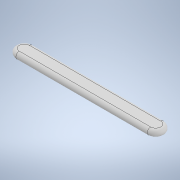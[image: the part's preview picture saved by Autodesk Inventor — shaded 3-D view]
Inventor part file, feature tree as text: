
AUTODESK INVENTOR PART (.ipt)
format: ipt  version: 2020 (Build 240168000, 168)  size: 114,688 bytes
history: native  units: in
note: dims shown in document units (in); Inventor stores cm internally (conversion verified against a paired STEP export)
features: fillet x2, extrude x1, sketch x1
ambient origin geometry x8: Origin, YZ Plane, XZ Plane, XY Plane, X Axis, Y Axis, Z Axis, Center Point
bodies: Solid1 (feature_tree)
feature tree (4):
  extrude  "Extrusion1"  Depth=0.0394in
  fillet  "Fillet1"  Radius=0.0787in
  fillet  "Fillet2"  Radius=0.0984in
  sketch  "Sketch1"  dims[d0=1.7323in d1=0.1969in d2=0.0787in d3=0.0in d4=0.0984in d5=0.0394in]
